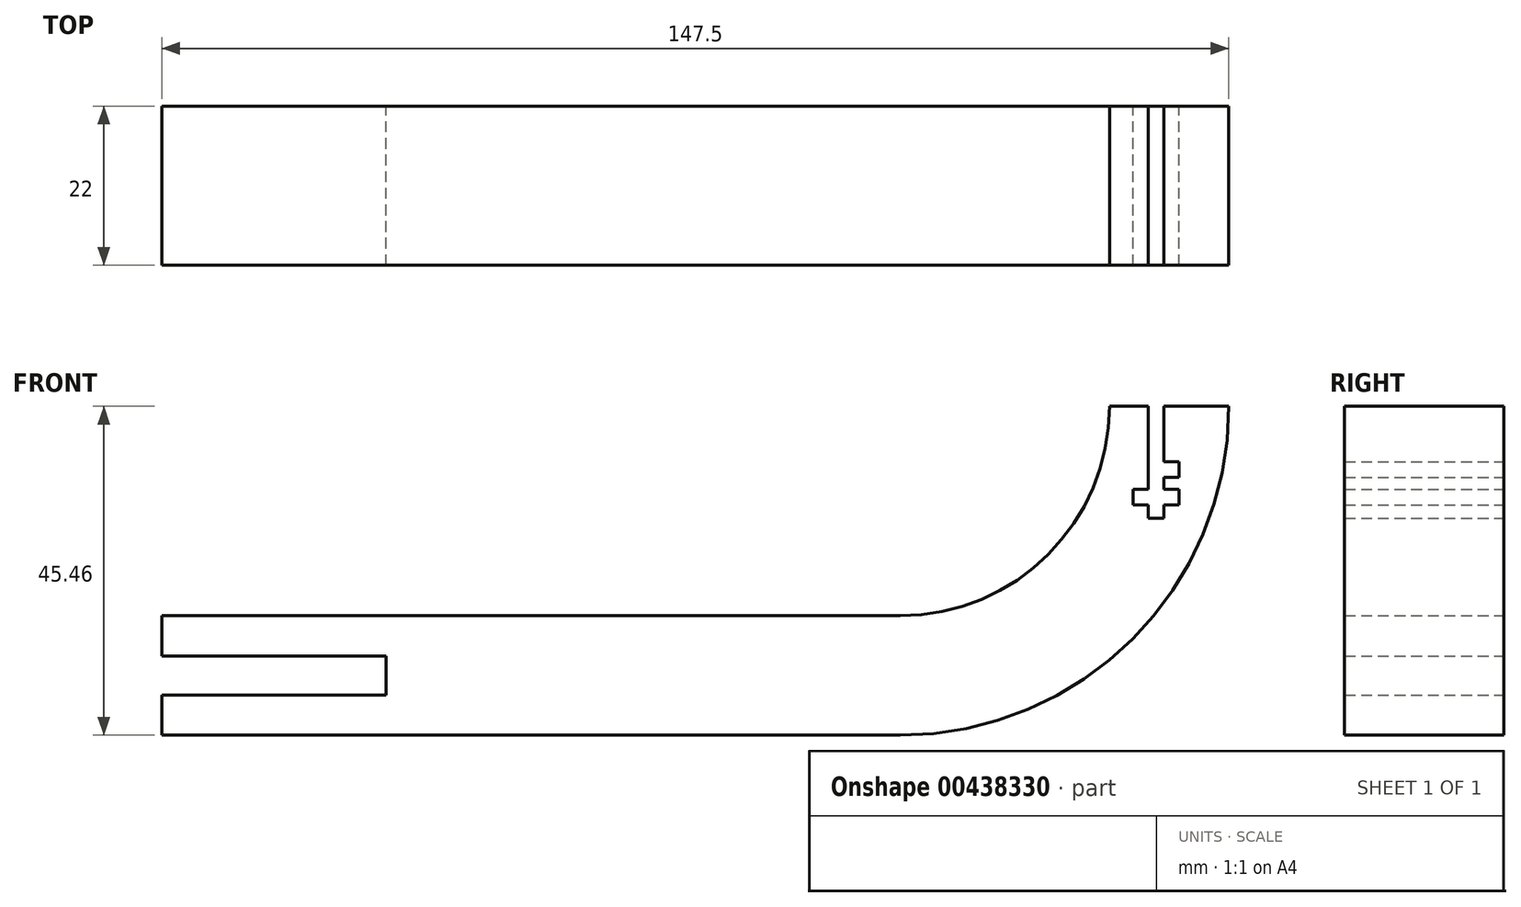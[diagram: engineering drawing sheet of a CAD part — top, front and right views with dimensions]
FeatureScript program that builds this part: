
annotation { "Feature Type Name" : "Feature", "Feature Type Description" : "" }
export const myFeature = defineFeature(function(context is Context, id is Id, definition is map)
    precondition{}
    {
        {
            var Q0;
            Q0=qCreatedBy(makeId("Front.planeOp"),FACE);
            var sketch = newSketch(context, id + "F0", { "sketchPlane" : qUnion([Q0])});
            skLineSegment(sketch, "E0.bottom", {"start": v(51.02, -8.25) * mm, "end": v(-51.02, -8.25) * mm});
            skLineSegment(sketch, "E0.top", {"start": v(51.02, 8.25) * mm, "end": v(-51.02, 8.25) * mm});
            skLineSegment(sketch, "E0.left", {"start": v(51.02, -8.25) * mm, "end": v(51.02, 8.25) * mm});
            skLineSegment(sketch, "E0.right", {"start": v(-51.02, -8.25) * mm, "end": v(-51.02, 8.25) * mm});
            skPoint(sketch, "E0.middle", {"position": v(0, 0) * mm});
            skLineSegment(sketch, "E1.bottom", {"start": v(-20.02, 2.7) * mm, "end": v(-82.02, 2.7) * mm});
            skLineSegment(sketch, "E1.top", {"start": v(-20.02, -2.7) * mm, "end": v(-82.02, -2.7) * mm});
            skLineSegment(sketch, "E1.left", {"start": v(-20.02, 2.7) * mm, "end": v(-20.02, -2.7) * mm});
            skLineSegment(sketch, "E1.right", {"start": v(-82.02, 2.7) * mm, "end": v(-82.02, -2.7) * mm});
            skPoint(sketch, "E1.middle", {"position": v(-51.02, 0) * mm});
            skArc(sketch, "E2", {"start": v(51.02, -8.25) * mm, "mid": v(83.17, 5.07) * mm, "end": v(96.48, 37.21) * mm});
            skArc(sketch, "E3.0", {"start": v(51.02, 8.25) * mm, "mid": v(71.5, 16.73) * mm, "end": v(79.98, 37.21) * mm});
            skLineSegment(sketch, "E4", {"start": v(79.98, 37.21) * mm, "end": v(96.48, 37.21) * mm});
            skPoint(sketch, "E5.oppositeSnap0", {"position": v(88.23, 37.21) * mm});
            skLineSegment(sketch, "E6", {"start": v(85.33, 40.06) * mm, "end": v(85.33, 25.71) * mm});
            skLineSegment(sketch, "E7", {"start": v(85.33, 25.71) * mm, "end": v(83.23, 25.71) * mm});
            skLineSegment(sketch, "E8", {"start": v(83.23, 25.71) * mm, "end": v(83.23, 23.56) * mm});
            skLineSegment(sketch, "E9", {"start": v(83.23, 23.56) * mm, "end": v(85.33, 23.56) * mm});
            skLineSegment(sketch, "E10", {"start": v(85.33, 23.56) * mm, "end": v(85.33, 21.76) * mm});
            skLineSegment(sketch, "E11", {"start": v(85.33, 21.76) * mm, "end": v(87.48, 21.76) * mm});
            skLineSegment(sketch, "E12", {"start": v(87.48, 40.06) * mm, "end": v(85.33, 40.06) * mm});
            skLineSegment(sketch, "E13", {"start": v(87.48, 40.06) * mm, "end": v(87.48, 29.54) * mm});
            skLineSegment(sketch, "E14", {"start": v(87.48, 29.54) * mm, "end": v(89.58, 29.54) * mm});
            skLineSegment(sketch, "E15", {"start": v(89.58, 29.54) * mm, "end": v(89.58, 27.39) * mm});
            skLineSegment(sketch, "E16", {"start": v(89.58, 27.39) * mm, "end": v(87.48, 27.39) * mm});
            skLineSegment(sketch, "E17", {"start": v(87.48, 27.39) * mm, "end": v(87.48, 25.71) * mm});
            skLineSegment(sketch, "E18", {"start": v(87.48, 25.71) * mm, "end": v(89.58, 25.71) * mm});
            skLineSegment(sketch, "E19", {"start": v(89.58, 25.71) * mm, "end": v(89.58, 23.56) * mm});
            skLineSegment(sketch, "E20", {"start": v(89.58, 23.56) * mm, "end": v(87.48, 23.56) * mm});
            skLineSegment(sketch, "E21", {"start": v(87.48, 23.56) * mm, "end": v(87.48, 21.76) * mm});
            skSolve(sketch);
        }
        {
            var Q0;
            {var subQ8=sQuery(id+"F0.wireOp",EDGE,"E0.bottom");Q0=makeQuery(id+"F0.imprint","IMPRINT",FACE,{"disambiguationData":[TD([[makeQuery(id+"F0.imprint","IMPRINT",EDGE,{"derivedFrom":subQ8}),-1.0]])]});}
            var Q1;
            {var subQ4=sQuery(id+"F0.wireOp",EDGE,"cvli10MZ-F9XX-AXS4-cFUv-hVWD5KjFyp10");Q1=makeQuery(id+"F0.imprint","IMPRINT",FACE,{"disambiguationData":[TD([[makeQuery(id+"F0.imprint","IMPRINT",EDGE,{"derivedFrom":subQ4}),1.0]])]});}
            var Q2;
            Q2=makeQuery(id+"F0.imprint","IMPRINT",FACE,{"disambiguationData":[TD([[makeQuery(id+"F0.imprint","IMPRINT",EDGE,{"derivedFrom":sQuery(id+"F0.wireOp",EDGE,"E0.left")}),-1.0]])]});
            extrude(context, id + "F1", {"entities" : qUnion([Q0, Q1, Q2]), "endBound" : BoundingType.SYMMETRIC, "depth" : 22 * mm, "offsetDistance" : 25 * mm});
        }
    });
